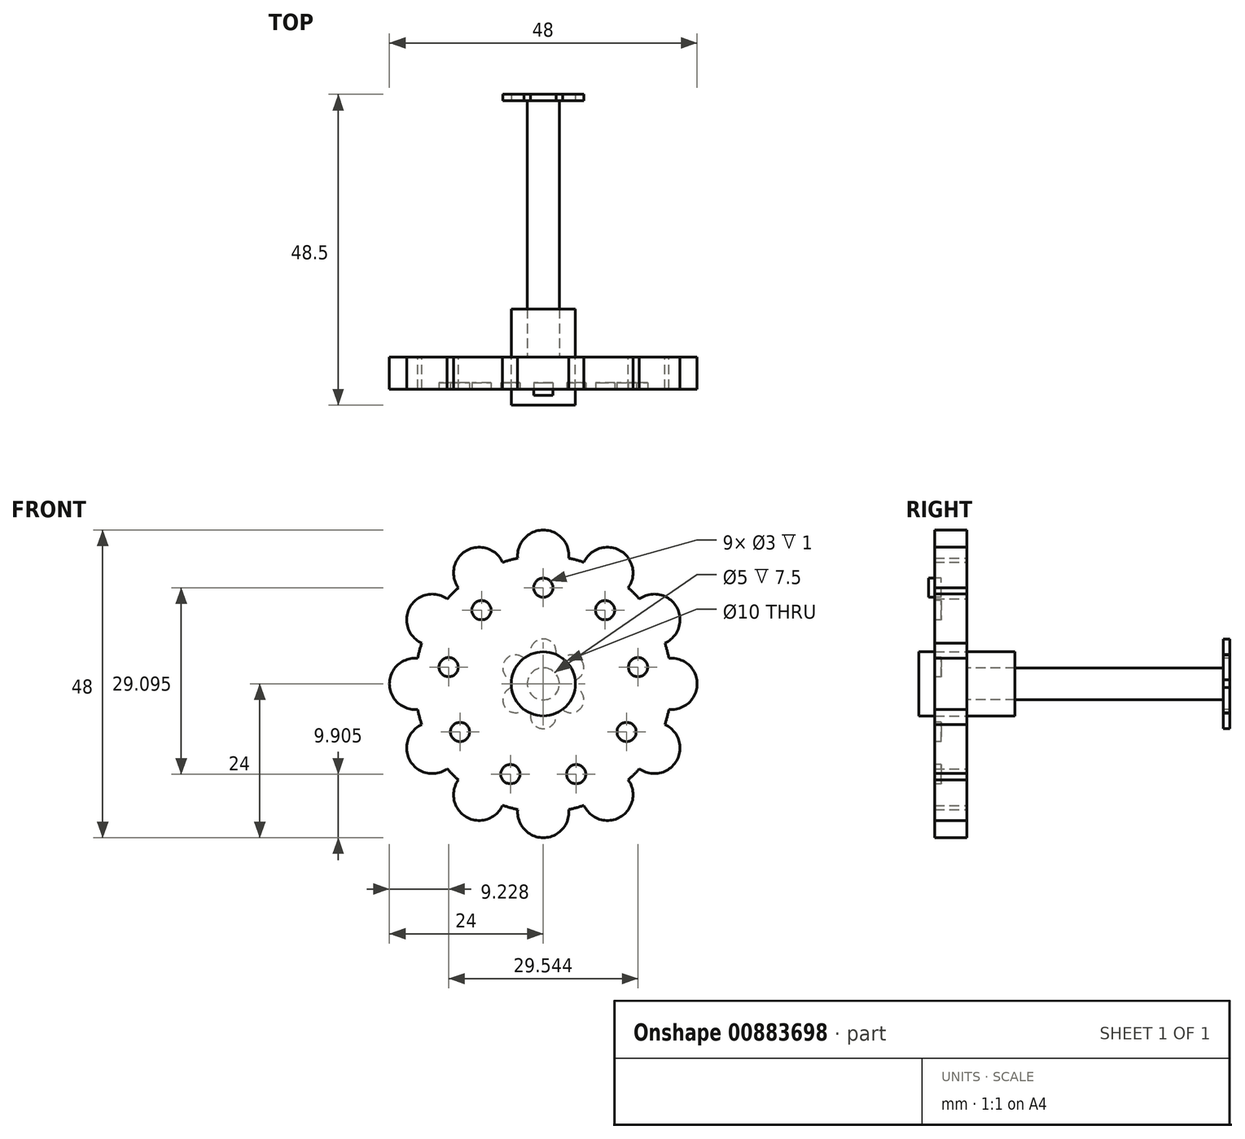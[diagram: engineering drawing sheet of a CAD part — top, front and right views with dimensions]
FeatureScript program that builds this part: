
annotation { "Feature Type Name" : "Feature", "Feature Type Description" : "" }
export const myFeature = defineFeature(function(context is Context, id is Id, definition is map)
    precondition{}
    {
        {
            var Q0;
            Q0=qCreatedBy(makeId("Front.planeOp"),FACE);
            var sketch = newSketch(context, id + "F0", { "sketchPlane" : qUnion([Q0])});
            skCircle(sketch, "E0", {"center": v(0, 0) * mm, "radius": 20 * mm});
            skCircle(sketch, "E1", {"center": v(0, 0) * mm, "radius": 5 * mm});
            skArc(sketch, "E2", {"start": v(3.98, 19.6) * mm, "mid": v(0, 24) * mm, "end": v(-3.98, 19.6) * mm});
            skArc(sketch, "E3.1.0", {"start": v(-6.35, 18.96) * mm, "mid": v(-12, 20.78) * mm, "end": v(-13.25, 14.98) * mm});
            skArc(sketch, "E3.2.0", {"start": v(-14.98, 13.25) * mm, "mid": v(-20.78, 12) * mm, "end": v(-18.96, 6.35) * mm});
            skArc(sketch, "E4.3.3.0", {"start": v(-19.6, 3.98) * mm, "mid": v(-24, 0) * mm, "end": v(-19.6, -3.98) * mm});
            skArc(sketch, "E4.3.4.0", {"start": v(-18.96, -6.35) * mm, "mid": v(-20.78, -12) * mm, "end": v(-14.98, -13.25) * mm});
            skArc(sketch, "E4.3.5.0", {"start": v(-13.25, -14.98) * mm, "mid": v(-12, -20.78) * mm, "end": v(-6.35, -18.96) * mm});
            skArc(sketch, "E4.3.6.0", {"start": v(-3.98, -19.6) * mm, "mid": v(0, -24) * mm, "end": v(3.98, -19.6) * mm});
            skArc(sketch, "E4.3.7.0", {"start": v(6.35, -18.96) * mm, "mid": v(12, -20.78) * mm, "end": v(13.25, -14.98) * mm});
            skArc(sketch, "E4.3.8.0", {"start": v(14.98, -13.25) * mm, "mid": v(20.78, -12) * mm, "end": v(18.96, -6.35) * mm});
            skArc(sketch, "E4.3.9.0", {"start": v(19.6, -3.98) * mm, "mid": v(24, 0) * mm, "end": v(19.6, 3.98) * mm});
            skArc(sketch, "E4.3.10.0", {"start": v(18.96, 6.35) * mm, "mid": v(20.78, 12) * mm, "end": v(14.98, 13.25) * mm});
            skArc(sketch, "E4.3.11.0", {"start": v(13.25, 14.98) * mm, "mid": v(12, 20.78) * mm, "end": v(6.35, 18.96) * mm});
            skSolve(sketch);
        }
        {
            var Q0;
            Q0 = qSketchRegion(id + "F0", true);
            extrude(context, id + "F1", {"entities" : qUnion([Q0]), "depth" : 5 * mm, "offsetDistance" : 25 * mm});
        }
        {
            var Q0;
            Q0=makeQuery(id+"F1.opExtrude","CAP_FACE",FACE,{"disambiguationData":[OSD([sQuery(id+"F0.wireOp",EDGE,"E0"),sQuery(id+"F0.wireOp",EDGE,"Q3HawSfr-Yc1m-u8ap-QaUd-JkndJFVzpWAL"),sQuery(id+"F0.wireOp",EDGE,"1H7idUGe-tVaQ-PfMa-Q3VK-DtBNIJ9UVp3s"),sQuery(id+"F0.wireOp",EDGE,"c086199f-d6aa-453d-9f93-155208173d3f0.MirrorCS"),sQuery(id+"F0.wireOp",EDGE,"98939027-4150-43ed-9ddd-95c83e1715170.MirrorCS"),sQuery(id+"F0.wireOp",EDGE,"4aadad1c-a26f-467f-b7ad-549becc40827.1.0"),sQuery(id+"F0.wireOp",EDGE,"4aadad1c-a26f-467f-b7ad-549becc40827.1.1"),sQuery(id+"F0.wireOp",EDGE,"4aadad1c-a26f-467f-b7ad-549becc40827.1.2"),sQuery(id+"F0.wireOp",EDGE,"4aadad1c-a26f-467f-b7ad-549becc40827.1.3"),sQuery(id+"F0.wireOp",EDGE,"4aadad1c-a26f-467f-b7ad-549becc40827.2.0"),sQuery(id+"F0.wireOp",EDGE,"4aadad1c-a26f-467f-b7ad-549becc40827.2.1"),sQuery(id+"F0.wireOp",EDGE,"4aadad1c-a26f-467f-b7ad-549becc40827.2.2"),sQuery(id+"F0.wireOp",EDGE,"4aadad1c-a26f-467f-b7ad-549becc40827.2.3"),sQuery(id+"F0.wireOp",EDGE,"32a6017c-9b45-4221-a417-20ed053f8597.2.3.0"),sQuery(id+"F0.wireOp",EDGE,"32a6017c-9b45-4221-a417-20ed053f8597.3.3.0"),sQuery(id+"F0.wireOp",EDGE,"32a6017c-9b45-4221-a417-20ed053f8597.6.3.0"),sQuery(id+"F0.wireOp",EDGE,"32a6017c-9b45-4221-a417-20ed053f8597.9.3.0"),sQuery(id+"F0.wireOp",EDGE,"32a6017c-9b45-4221-a417-20ed053f8597.2.4.0"),sQuery(id+"F0.wireOp",EDGE,"32a6017c-9b45-4221-a417-20ed053f8597.3.4.0"),sQuery(id+"F0.wireOp",EDGE,"32a6017c-9b45-4221-a417-20ed053f8597.6.4.0"),sQuery(id+"F0.wireOp",EDGE,"32a6017c-9b45-4221-a417-20ed053f8597.9.4.0"),sQuery(id+"F0.wireOp",EDGE,"32a6017c-9b45-4221-a417-20ed053f8597.2.5.0"),sQuery(id+"F0.wireOp",EDGE,"32a6017c-9b45-4221-a417-20ed053f8597.3.5.0"),sQuery(id+"F0.wireOp",EDGE,"32a6017c-9b45-4221-a417-20ed053f8597.6.5.0"),sQuery(id+"F0.wireOp",EDGE,"32a6017c-9b45-4221-a417-20ed053f8597.9.5.0"),sQuery(id+"F0.wireOp",EDGE,"32a6017c-9b45-4221-a417-20ed053f8597.2.6.0"),sQuery(id+"F0.wireOp",EDGE,"32a6017c-9b45-4221-a417-20ed053f8597.3.6.0"),sQuery(id+"F0.wireOp",EDGE,"32a6017c-9b45-4221-a417-20ed053f8597.6.6.0"),sQuery(id+"F0.wireOp",EDGE,"32a6017c-9b45-4221-a417-20ed053f8597.9.6.0"),sQuery(id+"F0.wireOp",EDGE,"32a6017c-9b45-4221-a417-20ed053f8597.2.7.0"),sQuery(id+"F0.wireOp",EDGE,"32a6017c-9b45-4221-a417-20ed053f8597.3.7.0"),sQuery(id+"F0.wireOp",EDGE,"32a6017c-9b45-4221-a417-20ed053f8597.6.7.0"),sQuery(id+"F0.wireOp",EDGE,"32a6017c-9b45-4221-a417-20ed053f8597.9.7.0"),sQuery(id+"F0.wireOp",EDGE,"32a6017c-9b45-4221-a417-20ed053f8597.2.8.0"),sQuery(id+"F0.wireOp",EDGE,"32a6017c-9b45-4221-a417-20ed053f8597.3.8.0"),sQuery(id+"F0.wireOp",EDGE,"32a6017c-9b45-4221-a417-20ed053f8597.6.8.0"),sQuery(id+"F0.wireOp",EDGE,"32a6017c-9b45-4221-a417-20ed053f8597.9.8.0"),sQuery(id+"F0.wireOp",EDGE,"E1")])],"isStart":false});
            var sketch = newSketch(context, id + "F2", { "sketchPlane" : qUnion([Q0])});
            skCircle(sketch, "E5", {"center": v(0, 15) * mm, "radius": 1.5 * mm});
            skSolve(sketch);
        }
        {
            var Q0;
            Q0 = qSketchRegion(id + "F2", true);
            extrude(context, id + "F3", {"entities" : qUnion([Q0]), "oppositeDirection" : true, "depth" : 1 * mm, "offsetDistance" : 25 * mm});
        }
        {
            var Q0;
            Q0=makeQuery(id+"F3.opExtrude","SWEPT_BODY",BODY,{"disambiguationData":[OSD([sQuery(id+"F2.wireOp",EDGE,"E5")])]});
            var Q1;
            Q1=makeQuery(id+"F1.opExtrude","CAP_EDGE",EDGE,{"disambiguationData":[OSD([sQuery(id+"F0.wireOp",EDGE,"E1")])],"isStart":false});
            circularPattern(context, id + "F4", {"entities" : qUnion([Q0]), "axis" : qUnion([Q1]), "angle" : 360 * degree, "instanceCount" : 9, "equalSpace" : true});
        }
        {
            var Q0;
            Q0=makeQuery(id+"F3.opExtrude","SWEPT_BODY",BODY,{"disambiguationData":[OSD([sQuery(id+"F2.wireOp",EDGE,"E5")])]});
            var Q1;
            Q1=makeQuery(id+"F4.opPattern","COPY",BODY,{"derivedFrom":makeQuery(id+"F3.opExtrude","SWEPT_BODY",BODY,{"disambiguationData":[OSD([sQuery(id+"F2.wireOp",EDGE,"E5")])]}),"instanceName":"1"});
            var Q2;
            Q2=makeQuery(id+"F4.opPattern","COPY",BODY,{"derivedFrom":makeQuery(id+"F3.opExtrude","SWEPT_BODY",BODY,{"disambiguationData":[OSD([sQuery(id+"F2.wireOp",EDGE,"E5")])]}),"instanceName":"2"});
            var Q3;
            Q3=makeQuery(id+"F4.opPattern","COPY",BODY,{"derivedFrom":makeQuery(id+"F3.opExtrude","SWEPT_BODY",BODY,{"disambiguationData":[OSD([sQuery(id+"F2.wireOp",EDGE,"E5")])]}),"instanceName":"3"});
            var Q4;
            Q4=makeQuery(id+"F4.opPattern","COPY",BODY,{"derivedFrom":makeQuery(id+"F3.opExtrude","SWEPT_BODY",BODY,{"disambiguationData":[OSD([sQuery(id+"F2.wireOp",EDGE,"E5")])]}),"instanceName":"4"});
            var Q5;
            Q5=makeQuery(id+"F4.opPattern","COPY",BODY,{"derivedFrom":makeQuery(id+"F3.opExtrude","SWEPT_BODY",BODY,{"disambiguationData":[OSD([sQuery(id+"F2.wireOp",EDGE,"E5")])]}),"instanceName":"5"});
            var Q6;
            Q6=makeQuery(id+"F4.opPattern","COPY",BODY,{"derivedFrom":makeQuery(id+"F3.opExtrude","SWEPT_BODY",BODY,{"disambiguationData":[OSD([sQuery(id+"F2.wireOp",EDGE,"E5")])]}),"instanceName":"6"});
            var Q7;
            Q7=makeQuery(id+"F4.opPattern","COPY",BODY,{"derivedFrom":makeQuery(id+"F3.opExtrude","SWEPT_BODY",BODY,{"disambiguationData":[OSD([sQuery(id+"F2.wireOp",EDGE,"E5")])]}),"instanceName":"7"});
            var Q8;
            Q8=makeQuery(id+"F4.opPattern","COPY",BODY,{"derivedFrom":makeQuery(id+"F3.opExtrude","SWEPT_BODY",BODY,{"disambiguationData":[OSD([sQuery(id+"F2.wireOp",EDGE,"E5")])]}),"instanceName":"8"});
            var Q9;
            Q9=makeQuery(id+"F1.opExtrude","SWEPT_BODY",BODY,{"disambiguationData":[OSD([sQuery(id+"F0.wireOp",EDGE,"E0"),sQuery(id+"F0.wireOp",EDGE,"Q3HawSfr-Yc1m-u8ap-QaUd-JkndJFVzpWAL"),sQuery(id+"F0.wireOp",EDGE,"1H7idUGe-tVaQ-PfMa-Q3VK-DtBNIJ9UVp3s"),sQuery(id+"F0.wireOp",EDGE,"c086199f-d6aa-453d-9f93-155208173d3f0.MirrorCS"),sQuery(id+"F0.wireOp",EDGE,"98939027-4150-43ed-9ddd-95c83e1715170.MirrorCS"),sQuery(id+"F0.wireOp",EDGE,"4aadad1c-a26f-467f-b7ad-549becc40827.1.0"),sQuery(id+"F0.wireOp",EDGE,"4aadad1c-a26f-467f-b7ad-549becc40827.1.1"),sQuery(id+"F0.wireOp",EDGE,"4aadad1c-a26f-467f-b7ad-549becc40827.1.2"),sQuery(id+"F0.wireOp",EDGE,"4aadad1c-a26f-467f-b7ad-549becc40827.1.3"),sQuery(id+"F0.wireOp",EDGE,"4aadad1c-a26f-467f-b7ad-549becc40827.2.0"),sQuery(id+"F0.wireOp",EDGE,"4aadad1c-a26f-467f-b7ad-549becc40827.2.1"),sQuery(id+"F0.wireOp",EDGE,"4aadad1c-a26f-467f-b7ad-549becc40827.2.2"),sQuery(id+"F0.wireOp",EDGE,"4aadad1c-a26f-467f-b7ad-549becc40827.2.3"),sQuery(id+"F0.wireOp",EDGE,"32a6017c-9b45-4221-a417-20ed053f8597.2.3.0"),sQuery(id+"F0.wireOp",EDGE,"32a6017c-9b45-4221-a417-20ed053f8597.3.3.0"),sQuery(id+"F0.wireOp",EDGE,"32a6017c-9b45-4221-a417-20ed053f8597.6.3.0"),sQuery(id+"F0.wireOp",EDGE,"32a6017c-9b45-4221-a417-20ed053f8597.9.3.0"),sQuery(id+"F0.wireOp",EDGE,"32a6017c-9b45-4221-a417-20ed053f8597.2.4.0"),sQuery(id+"F0.wireOp",EDGE,"32a6017c-9b45-4221-a417-20ed053f8597.3.4.0"),sQuery(id+"F0.wireOp",EDGE,"32a6017c-9b45-4221-a417-20ed053f8597.6.4.0"),sQuery(id+"F0.wireOp",EDGE,"32a6017c-9b45-4221-a417-20ed053f8597.9.4.0"),sQuery(id+"F0.wireOp",EDGE,"32a6017c-9b45-4221-a417-20ed053f8597.2.5.0"),sQuery(id+"F0.wireOp",EDGE,"32a6017c-9b45-4221-a417-20ed053f8597.3.5.0"),sQuery(id+"F0.wireOp",EDGE,"32a6017c-9b45-4221-a417-20ed053f8597.6.5.0"),sQuery(id+"F0.wireOp",EDGE,"32a6017c-9b45-4221-a417-20ed053f8597.9.5.0"),sQuery(id+"F0.wireOp",EDGE,"32a6017c-9b45-4221-a417-20ed053f8597.2.6.0"),sQuery(id+"F0.wireOp",EDGE,"32a6017c-9b45-4221-a417-20ed053f8597.3.6.0"),sQuery(id+"F0.wireOp",EDGE,"32a6017c-9b45-4221-a417-20ed053f8597.6.6.0"),sQuery(id+"F0.wireOp",EDGE,"32a6017c-9b45-4221-a417-20ed053f8597.9.6.0"),sQuery(id+"F0.wireOp",EDGE,"32a6017c-9b45-4221-a417-20ed053f8597.2.7.0"),sQuery(id+"F0.wireOp",EDGE,"32a6017c-9b45-4221-a417-20ed053f8597.3.7.0"),sQuery(id+"F0.wireOp",EDGE,"32a6017c-9b45-4221-a417-20ed053f8597.6.7.0"),sQuery(id+"F0.wireOp",EDGE,"32a6017c-9b45-4221-a417-20ed053f8597.9.7.0"),sQuery(id+"F0.wireOp",EDGE,"32a6017c-9b45-4221-a417-20ed053f8597.2.8.0"),sQuery(id+"F0.wireOp",EDGE,"32a6017c-9b45-4221-a417-20ed053f8597.3.8.0"),sQuery(id+"F0.wireOp",EDGE,"32a6017c-9b45-4221-a417-20ed053f8597.6.8.0"),sQuery(id+"F0.wireOp",EDGE,"32a6017c-9b45-4221-a417-20ed053f8597.9.8.0"),sQuery(id+"F0.wireOp",EDGE,"E1")])]});
            booleanBodies(context, id + "F5", {"operationType" : BooleanOperationType.SUBTRACTION, "tools" : qUnion([Q0, Q1, Q2, Q3, Q4, Q5, Q6, Q7, Q8]), "targets" : qUnion([Q9])});
        }
        {
            var Q0;
            Q0=makeQuery(id+"F5.opBoolean","COPY",FACE,{"derivedFrom":makeQuery(id+"F3.opExtrude","CAP_FACE",FACE,{"disambiguationData":[OSD([sQuery(id+"F2.wireOp",EDGE,"E5")])],"isStart":false})});
            var sketch = newSketch(context, id + "F6", { "sketchPlane" : qUnion([Q0])});
            skCircle(sketch, "E6", {"center": v(0, 15) * mm, "radius": 1.5 * mm});
            skSolve(sketch);
        }
        {
            var Q0;
            Q0 = qSketchRegion(id + "F6", true);
            extrude(context, id + "F7", {"entities" : qUnion([Q0]), "depth" : 2 * mm, "offsetDistance" : 25 * mm});
        }
        {
            var Q0;
            Q0=qCreatedBy(makeId("Front.planeOp"),FACE);
            var sketch = newSketch(context, id + "F8", { "sketchPlane" : qUnion([Q0])});
            skCircle(sketch, "E7", {"center": v(0, 0) * mm, "radius": 5 * mm});
            skSolve(sketch);
        }
        {
            var Q0;
            Q0 = qSketchRegion(id + "F8", true);
            extrude(context, id + "F9", {"entities" : qUnion([Q0]), "endBound" : BoundingType.SYMMETRIC, "depth" : 15 * mm, "offsetDistance" : 25 * mm});
        }
        {
            var Q0;
            Q0=qCreatedBy(makeId("Front.planeOp"),FACE);
            var sketch = newSketch(context, id + "F10", { "sketchPlane" : qUnion([Q0])});
            skCircle(sketch, "E8", {"center": v(0, 0) * mm, "radius": 2.5 * mm});
            skSolve(sketch);
        }
        {
            var Q0;
            Q0 = qSketchRegion(id + "F10", true);
            extrude(context, id + "F11", {"entities" : qUnion([Q0]), "oppositeDirection" : true, "depth" : 40 * mm, "offsetDistance" : 25 * mm});
        }
        {
            var Q0;
            Q0=makeQuery(id+"F11.opExtrude","CAP_FACE",FACE,{"disambiguationData":[OSD([sQuery(id+"F10.wireOp",EDGE,"E8")])],"isStart":false});
            var sketch = newSketch(context, id + "F12", { "sketchPlane" : qUnion([Q0])});
            skCircle(sketch, "E9", {"center": v(0, 0) * mm, "radius": 5 * mm});
            skArc(sketch, "E10", {"start": v(1.96, 4.6) * mm, "mid": v(0, 7) * mm, "end": v(-1.96, 4.6) * mm});
            skArc(sketch, "E11.1.0", {"start": v(-3, 4) * mm, "mid": v(-6.06, 3.5) * mm, "end": v(-4.96, 0.6) * mm});
            skArc(sketch, "E11.2.0", {"start": v(-4.96, -0.6) * mm, "mid": v(-6.06, -3.5) * mm, "end": v(-3, -4) * mm});
            skArc(sketch, "E12.3.3.0", {"start": v(-1.96, -4.6) * mm, "mid": v(0, -7) * mm, "end": v(1.96, -4.6) * mm});
            skArc(sketch, "E12.3.4.0", {"start": v(3, -4) * mm, "mid": v(6.06, -3.5) * mm, "end": v(4.96, -0.6) * mm});
            skArc(sketch, "E13.3.5.0", {"start": v(4.96, 0.6) * mm, "mid": v(6.06, 3.5) * mm, "end": v(3, 4) * mm});
            skSolve(sketch);
        }
        {
            var Q0;
            Q0 = qSketchRegion(id + "F12", true);
            extrude(context, id + "F13", {"entities" : qUnion([Q0]), "operationType" : NewBodyOperationType.ADD, "depth" : 1 * mm, "offsetDistance" : 25 * mm});
        }
        {
            var Q0;
            Q0=makeQuery(id+"F11.opExtrude","SWEPT_BODY",BODY,{"disambiguationData":[OSD([sQuery(id+"F10.wireOp",EDGE,"E8")])]});
            var Q1;
            Q1=makeQuery(id+"F9.opExtrude","SWEPT_BODY",BODY,{"disambiguationData":[OSD([sQuery(id+"F8.wireOp",EDGE,"E7")])]});
            booleanBodies(context, id + "F14", {"operationType" : BooleanOperationType.SUBTRACTION, "tools" : qUnion([Q0]), "targets" : qUnion([Q1]), "keepTools" : true});
        }
    });
